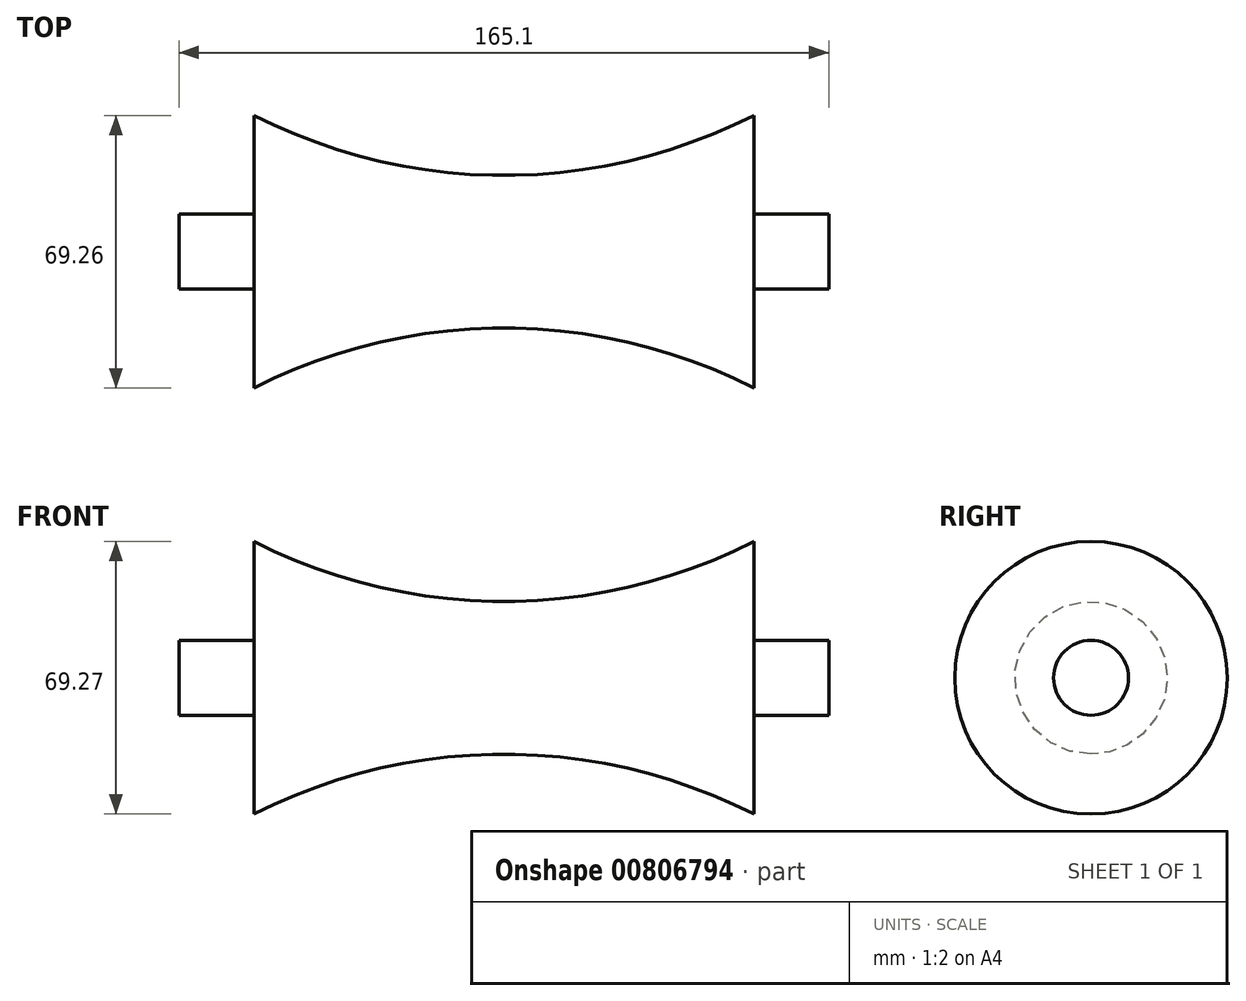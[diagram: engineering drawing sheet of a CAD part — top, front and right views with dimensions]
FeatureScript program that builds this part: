
annotation { "Feature Type Name" : "Feature", "Feature Type Description" : "" }
export const myFeature = defineFeature(function(context is Context, id is Id, definition is map)
    precondition{}
    {
        {
            var Q0;
            Q0=qCreatedBy(makeId("Front.planeOp"),FACE);
            var sketch = newSketch(context, id + "F0", { "sketchPlane" : qUnion([Q0])});
            skArc(sketch, "E0", {"start": v(-63.5, 0) * mm, "mid": v(0, -15.24) * mm, "end": v(63.5, 0) * mm});
            skLineSegment(sketch, "E1", {"start": v(63.5, 0) * mm, "end": v(63.5, -34.63) * mm});
            skLineSegment(sketch, "E2", {"start": v(63.5, -34.63) * mm, "end": v(-63.5, -34.63) * mm});
            skLineSegment(sketch, "E3", {"start": v(-63.5, -34.63) * mm, "end": v(-63.5, 0) * mm});
            skSolve(sketch);
        }
        {
            var Q0;
            Q0 = qSketchRegion(id + "F0", true);
            var Q1;
            Q1=sQuery(id+"F0.wireOp",EDGE,"E2");
            revolve(context, id + "F1", {"surfaceOperationType" : NewSurfaceOperationType.NEW, "entities" : qUnion([Q0]), "axis" : qUnion([Q1]), "revolveType" : RevolveType.FULL});
        }
        {
            var Q0;
            Q0=makeQuery(id+"F1.opRevolve","SWEPT_FACE",FACE,{"disambiguationData":[OSD([sQuery(id+"F0.wireOp",EDGE,"E3")])]});
            var sketch = newSketch(context, id + "F2", { "sketchPlane" : qUnion([Q0])});
            skCircle(sketch, "E4", {"center": v(0, -34.63) * mm, "radius": 9.53 * mm});
            skSolve(sketch);
        }
        {
            var Q0;
            Q0 = qSketchRegion(id + "F2", true);
            extrude(context, id + "F3", {"entities" : qUnion([Q0]), "operationType" : NewBodyOperationType.ADD, "depth" : 19.05 * mm, "offsetDistance" : 25.4 * mm});
        }
        {
            var Q0;
            Q0=makeQuery(id+"F1.opRevolve","SWEPT_FACE",FACE,{"disambiguationData":[OSD([sQuery(id+"F0.wireOp",EDGE,"E1")])]});
            var sketch = newSketch(context, id + "F4", { "sketchPlane" : qUnion([Q0])});
            skCircle(sketch, "E5", {"center": v(0, -34.63) * mm, "radius": 9.53 * mm});
            skSolve(sketch);
        }
        {
            var Q0;
            Q0 = qSketchRegion(id + "F4", true);
            extrude(context, id + "F5", {"entities" : qUnion([Q0]), "operationType" : NewBodyOperationType.ADD, "depth" : 19.05 * mm, "offsetDistance" : 25.4 * mm});
        }
    });
